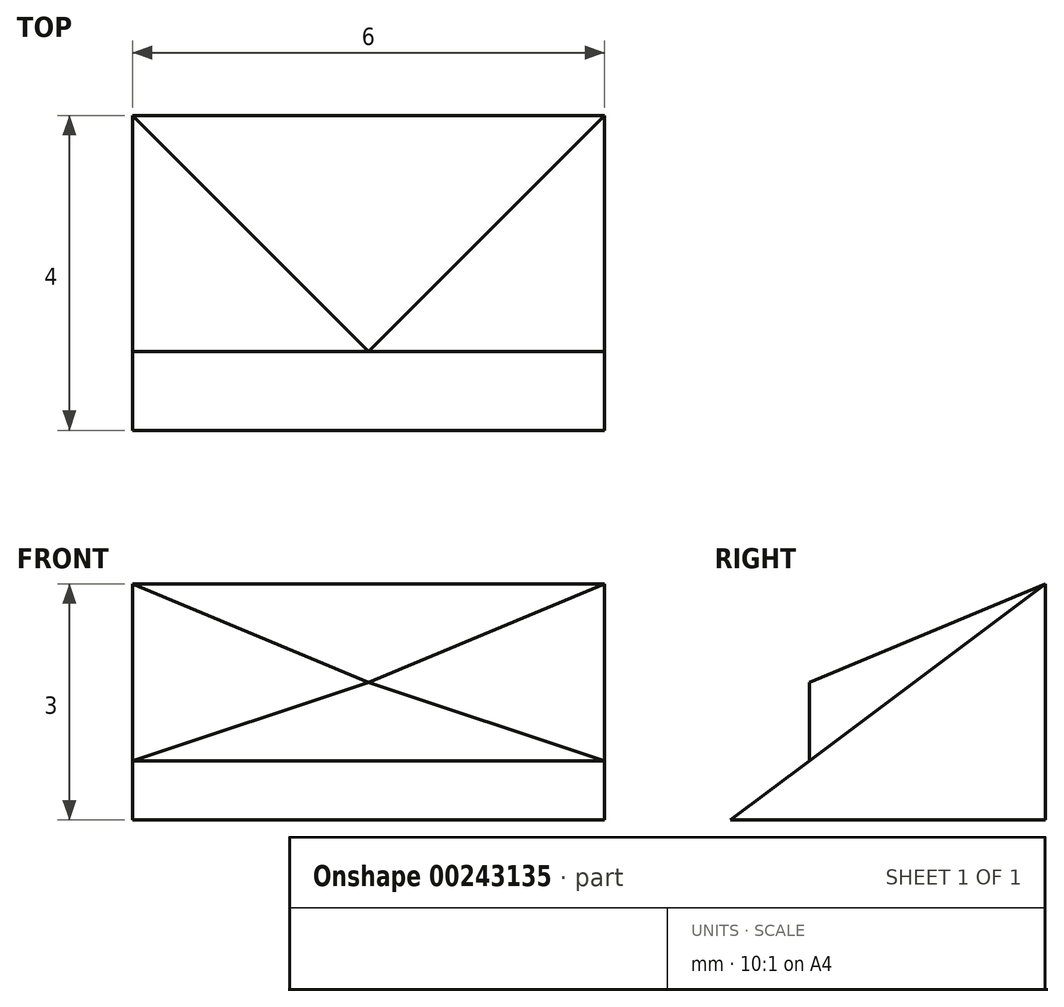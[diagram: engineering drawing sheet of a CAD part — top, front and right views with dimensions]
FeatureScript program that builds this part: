
annotation { "Feature Type Name" : "Feature", "Feature Type Description" : "" }
export const myFeature = defineFeature(function(context is Context, id is Id, definition is map)
    precondition{}
    {
        {
            var Q0;
            Q0=qCreatedBy(makeId("Right.planeOp"),FACE);
            var sketch = newSketch(context, id + "F0", { "sketchPlane" : qUnion([Q0])});
            skLineSegment(sketch, "E0", {"start": v(0, 0) * mm, "end": v(4, 0) * mm});
            skLineSegment(sketch, "E1", {"start": v(4, 0) * mm, "end": v(4, 3) * mm});
            skLineSegment(sketch, "E2", {"start": v(4, 3) * mm, "end": v(0, 0) * mm});
            skSolve(sketch);
        }
        {
            var Q0;
            Q0 = qSketchRegion(id + "F0", true);
            extrude(context, id + "F1", {"entities" : qUnion([Q0]), "depth" : 6 * mm});
        }
        {
            var Q0;
            Q0=makeQuery(id+"F1.opExtrude","CAP_FACE",FACE,{"disambiguationData":[OSD([sQuery(id+"F0.wireOp",EDGE,"E0"),sQuery(id+"F0.wireOp",EDGE,"E1"),sQuery(id+"F0.wireOp",EDGE,"E2")])],"isStart":false});
            var sketch = newSketch(context, id + "F2", { "sketchPlane" : qUnion([Q0])});
            skLineSegment(sketch, "E3", {"start": v(0, 0) * mm, "end": v(1, 0) * mm});
            skLineSegment(sketch, "E4", {"start": v(1, 0) * mm, "end": v(1, 0.75) * mm});
            skSolve(sketch);
        }
        {
            var Q0;
            Q0=makeQuery(id+"F1.opExtrude","SWEPT_FACE",FACE,{"disambiguationData":[OSD([sQuery(id+"F0.wireOp",EDGE,"E2")])]});
            var sketch = newSketch(context, id + "F3", { "sketchPlane" : qUnion([Q0])});
            skPoint(sketch, "E5.0", {"position": v(6, 1.25) * mm});
            skLineSegment(sketch, "E6", {"start": v(6, 1.25) * mm, "end": v(0, 1.25) * mm});
            skSolve(sketch);
        }
        {
            var Q0;
            Q0=sQuery(id+"F2.wireOp",VERTEX,"E4.start");
            var Q1;
            Q1=sQuery(id+"F3.wireOp",VERTEX,"E5.0");
            var Q2;
            Q2=sQuery(id+"F3.wireOp",VERTEX,"E6.end");
            cPlane(context, id + "F4", {"entities" : qUnion([Q0, Q1, Q2]), "cplaneType" : CPlaneType.THREE_POINT, "offset" : 25 * mm, "width" : 150 * mm, "height" : 150 * mm});
        }
        {
            var Q0;
            Q0=qCreatedBy(id+"F4.planeOp",FACE);
            var sketch = newSketch(context, id + "F5", { "sketchPlane" : qUnion([Q0])});
            skPoint(sketch, "E7.0", {"position": v(0, 0.75) * mm});
            skPoint(sketch, "E8.0", {"position": v(-6, 0.75) * mm});
            skLineSegment(sketch, "E9", {"start": v(0, 0.75) * mm, "end": v(-6, 0.75) * mm});
            skLineSegment(sketch, "E10", {"start": v(-3, 0.75) * mm, "end": v(-3, 1.75) * mm, "construction": true});
            skLineSegment(sketch, "E11", {"start": v(-3, 1.75) * mm, "end": v(0, 0.75) * mm});
            skLineSegment(sketch, "E12", {"start": v(-3, 1.75) * mm, "end": v(-6, 0.75) * mm});
            skSolve(sketch);
        }
        {
            var Q0;
            Q0=makeQuery(id+"F1.opExtrude","CAP_VERTEX",VERTEX,{"disambiguationData":[OSD([sQuery(id+"F0.wireOp",EDGE,"E1"),sQuery(id+"F0.wireOp",EDGE,"E2")])],"isStart":true});
            var Q1;
            Q1=sQuery(id+"F5.wireOp",VERTEX,"E12.start");
            var Q2;
            Q2=sQuery(id+"F5.wireOp",VERTEX,"E7.0");
            cPlane(context, id + "F6", {"entities" : qUnion([Q0, Q1, Q2]), "cplaneType" : CPlaneType.THREE_POINT, "offset" : 25 * mm, "width" : 150 * mm, "height" : 150 * mm});
        }
        {
            var Q0;
            Q0=qCreatedBy(id+"F6.planeOp",FACE);
            var sketch = newSketch(context, id + "F7", { "sketchPlane" : qUnion([Q0])});
            skPoint(sketch, "E13.0", {"position": v(0, 5) * mm});
            skPoint(sketch, "E13.1", {"position": v(3.1, 1.85) * mm});
            skPoint(sketch, "E13.2", {"position": v(0, 1.25) * mm});
            skLineSegment(sketch, "E14", {"start": v(0, 5) * mm, "end": v(3.1, 1.85) * mm});
            skLineSegment(sketch, "E15", {"start": v(3.1, 1.85) * mm, "end": v(0, 1.25) * mm});
            skLineSegment(sketch, "E16", {"start": v(0, 1.25) * mm, "end": v(0, 5) * mm});
            skSolve(sketch);
        }
        {
            var Q0;
            Q0=sQuery(id+"F7.wireOp",VERTEX,"E13.1");
            var Q1;
            Q1=sQuery(id+"F5.wireOp",VERTEX,"E8.0");
            var Q2;
            Q2=makeQuery(id+"F1.opExtrude","CAP_VERTEX",VERTEX,{"disambiguationData":[OSD([sQuery(id+"F0.wireOp",EDGE,"E1"),sQuery(id+"F0.wireOp",EDGE,"E2")])],"isStart":false});
            cPlane(context, id + "F8", {"entities" : qUnion([Q0, Q1, Q2]), "cplaneType" : CPlaneType.THREE_POINT, "offset" : 25 * mm, "width" : 150 * mm, "height" : 150 * mm});
        }
        {
            var Q0;
            Q0=qCreatedBy(id+"F8.planeOp",FACE);
            var sketch = newSketch(context, id + "F9", { "sketchPlane" : qUnion([Q0])});
            skPoint(sketch, "E17.0", {"position": v(5.8, -5) * mm});
            skPoint(sketch, "E17.1", {"position": v(2.7, -1.85) * mm});
            skPoint(sketch, "E17.2", {"position": v(5.8, -1.25) * mm});
            skLineSegment(sketch, "E18", {"start": v(2.7, -1.85) * mm, "end": v(5.8, -5) * mm});
            skLineSegment(sketch, "E19", {"start": v(5.8, -1.25) * mm, "end": v(2.7, -1.85) * mm});
            skLineSegment(sketch, "E20", {"start": v(5.8, -5) * mm, "end": v(5.8, -1.25) * mm});
            skSolve(sketch);
        }
        {
            var Q0;
            {var subQ0=sQuery(id+"F2.wireOp",EDGE,"E4");Q0=makeQuery(id+"F2.imprint","IMPRINT",FACE,{"disambiguationData":[TD([[makeQuery(id+"F2.imprint","IMPRINT",EDGE,{"derivedFrom":subQ0}),-1.0]])]});}
            var sketch = newSketch(context, id + "F10", { "sketchPlane" : qUnion([Q0])});
            skPoint(sketch, "E21.0", {"position": v(4, 3) * mm});
            skPoint(sketch, "E22.0", {"position": v(1, 0.75) * mm});
            skPoint(sketch, "E23.0", {"position": v(1, 1.75) * mm});
            skLineSegment(sketch, "E24", {"start": v(1, 0.75) * mm, "end": v(1, 1.75) * mm});
            skLineSegment(sketch, "E25", {"start": v(4, 3) * mm, "end": v(1, 1.75) * mm});
            skLineSegment(sketch, "E26", {"start": v(1, 0.75) * mm, "end": v(4, 3) * mm});
            skSolve(sketch);
        }
        {
            var Q0;
            Q0 = qSketchRegion(id + "F10", true);
            extrude(context, id + "F11", {"entities" : qUnion([Q0]), "operationType" : NewBodyOperationType.ADD, "oppositeDirection" : true, "depth" : 6 * mm});
        }
        {
            var Q0;
            Q0 = qSketchRegion(id + "F9", true);
            extrude(context, id + "F12", {"entities" : qUnion([Q0]), "operationType" : NewBodyOperationType.REMOVE, "oppositeDirection" : true, "depth" : 25 * mm});
        }
        {
            var Q0;
            Q0 = qSketchRegion(id + "F7", true);
            extrude(context, id + "F13", {"entities" : qUnion([Q0]), "operationType" : NewBodyOperationType.REMOVE, "depth" : 25 * mm});
        }
    });
